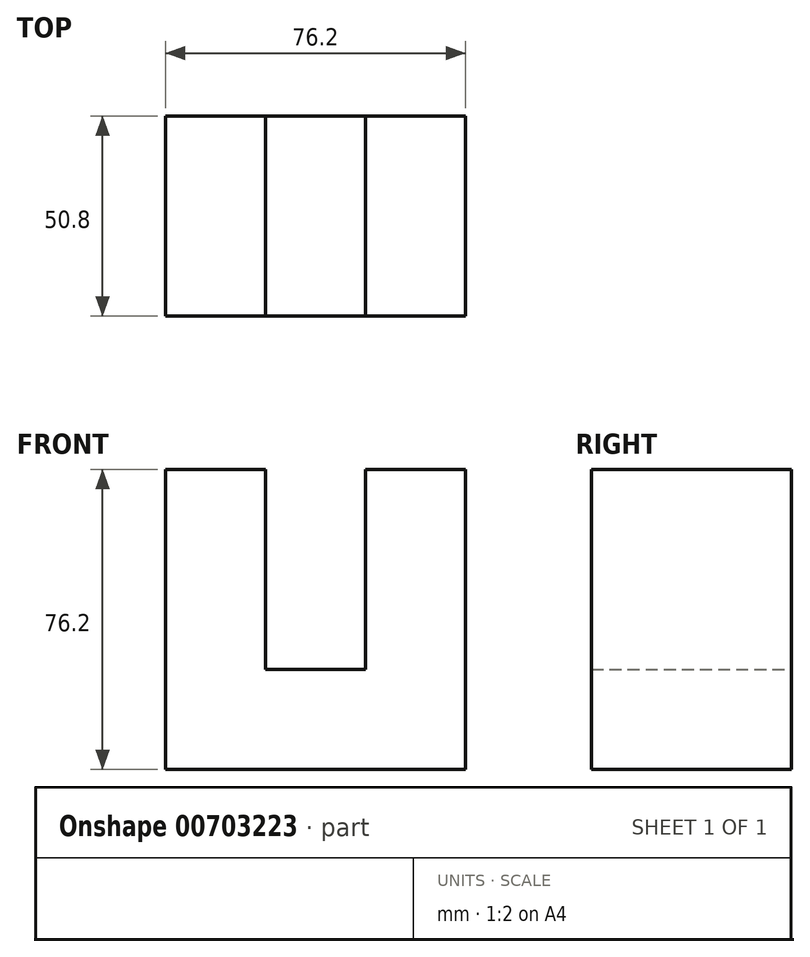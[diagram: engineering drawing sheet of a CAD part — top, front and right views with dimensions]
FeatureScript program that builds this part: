
annotation { "Feature Type Name" : "Feature", "Feature Type Description" : "" }
export const myFeature = defineFeature(function(context is Context, id is Id, definition is map)
    precondition{}
    {
        {
            var Q0;
            Q0=qCreatedBy(makeId("Front.planeOp"),FACE);
            var sketch = newSketch(context, id + "F0", { "sketchPlane" : qUnion([Q0])});
            skLineSegment(sketch, "E0", {"start": v(31.42, -14.6) * mm, "end": v(-44.78, -14.6) * mm});
            skLineSegment(sketch, "E1", {"start": v(-44.78, -14.6) * mm, "end": v(-44.78, 61.6) * mm});
            skLineSegment(sketch, "E2", {"start": v(-44.78, 61.6) * mm, "end": v(-19.38, 61.6) * mm});
            skLineSegment(sketch, "E3", {"start": v(-19.38, 61.6) * mm, "end": v(-19.38, 10.8) * mm});
            skLineSegment(sketch, "E4", {"start": v(-19.38, 10.8) * mm, "end": v(6.02, 10.8) * mm});
            skLineSegment(sketch, "E5", {"start": v(6.02, 10.8) * mm, "end": v(6.02, 61.6) * mm});
            skLineSegment(sketch, "E6", {"start": v(6.02, 61.6) * mm, "end": v(31.42, 61.6) * mm});
            skLineSegment(sketch, "E7", {"start": v(31.42, 61.6) * mm, "end": v(31.42, -14.6) * mm});
            skSolve(sketch);
        }
        {
            var Q0;
            Q0 = qSketchRegion(id + "F0", true);
            extrude(context, id + "F1", {"entities" : qUnion([Q0]), "depth" : 50.8 * mm, "offsetDistance" : 25.4 * mm});
        }
    });
